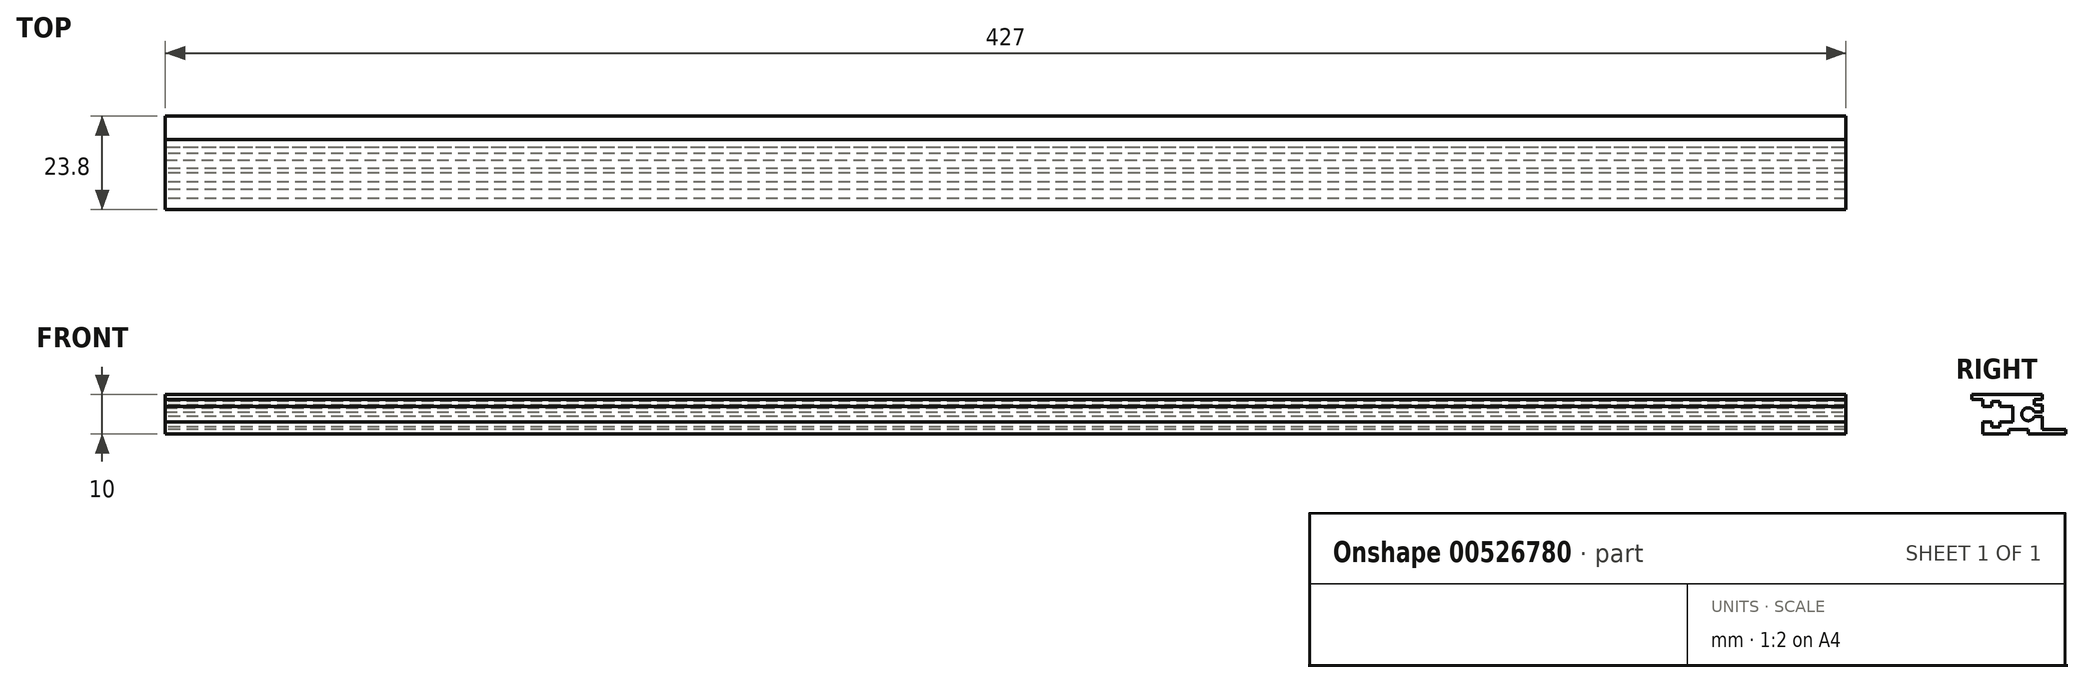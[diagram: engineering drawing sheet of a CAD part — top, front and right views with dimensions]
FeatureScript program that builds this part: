
annotation { "Feature Type Name" : "Feature", "Feature Type Description" : "" }
export const myFeature = defineFeature(function(context is Context, id is Id, definition is map)
    precondition{}
    {
        {
            assignVariable(context, id + "F0", {"name" : "length", "anyValue" : 427});
        }
        {
            var Q0;
            Q0=qCreatedBy(makeId("Right.planeOp"),FACE);
            var sketch = newSketch(context, id + "F1", { "sketchPlane" : qUnion([Q0])});
            skLineSegment(sketch, "E0.top", {"start": v(-37.38, 18.75) * mm, "end": v(-34.58, 18.75) * mm});
            skLineSegment(sketch, "E1", {"start": v(-37.38, 19.95) * mm, "end": v(-37.38, 18.75) * mm});
            skLineSegment(sketch, "E2.top", {"start": v(-13.58, 11.15) * mm, "end": v(-19.58, 11.15) * mm});
            skLineSegment(sketch, "E3", {"start": v(-37.38, 19.95) * mm, "end": v(-19.58, 19.95) * mm});
            skLineSegment(sketch, "E4", {"start": v(-13.58, 11.15) * mm, "end": v(-13.58, 9.95) * mm});
            skLineSegment(sketch, "E5.bottom", {"start": v(-19.58, 19.95) * mm, "end": v(-21.58, 19.95) * mm});
            skLineSegment(sketch, "E5.top", {"start": v(-19.58, 18.75) * mm, "end": v(-21.58, 18.75) * mm});
            skLineSegment(sketch, "E5.left", {"start": v(-19.58, 19.95) * mm, "end": v(-19.58, 18.75) * mm});
            skLineSegment(sketch, "E6.bottom", {"start": v(-21.58, 18.75) * mm, "end": v(-19.58, 18.75) * mm});
            skLineSegment(sketch, "E6.top", {"start": v(-21.58, 17.35) * mm, "end": v(-19.58, 17.35) * mm});
            skLineSegment(sketch, "E6.left", {"start": v(-21.58, 18.75) * mm, "end": v(-21.58, 17.35) * mm});
            skLineSegment(sketch, "E7.right", {"start": v(-26.98, 12.95) * mm, "end": v(-26.98, 16.95) * mm});
            skLineSegment(sketch, "E8", {"start": v(-34.58, 18.75) * mm, "end": v(-34.58, 16.95) * mm});
            skLineSegment(sketch, "E9.bottom", {"start": v(-34.58, 12.95) * mm, "end": v(-32.32, 12.95) * mm});
            skLineSegment(sketch, "E9.right", {"start": v(-32.32, 12.95) * mm, "end": v(-32.32, 11.7) * mm});
            skLineSegment(sketch, "E10.bottom", {"start": v(-32.32, 11.7) * mm, "end": v(-30.33, 11.7) * mm});
            skLineSegment(sketch, "E10.top", {"start": v(-32.32, 18.2) * mm, "end": v(-30.33, 18.2) * mm});
            skLineSegment(sketch, "E11", {"start": v(-34.58, 12.95) * mm, "end": v(-34.58, 9.95) * mm});
            skLineSegment(sketch, "E12", {"start": v(-34.58, 16.95) * mm, "end": v(-32.32, 16.95) * mm});
            skLineSegment(sketch, "E13", {"start": v(-26.98, 16.95) * mm, "end": v(-30.33, 16.95) * mm});
            skLineSegment(sketch, "E14", {"start": v(-32.32, 18.2) * mm, "end": v(-32.32, 16.95) * mm});
            skLineSegment(sketch, "E15", {"start": v(-26.98, 12.95) * mm, "end": v(-30.33, 12.95) * mm});
            skLineSegment(sketch, "E16", {"start": v(-30.33, 18.2) * mm, "end": v(-30.33, 16.95) * mm});
            skLineSegment(sketch, "E17", {"start": v(-30.33, 12.95) * mm, "end": v(-30.33, 11.7) * mm});
            skLineSegment(sketch, "E18.bottom", {"start": v(-19.58, 15.55) * mm, "end": v(-21.58, 15.55) * mm});
            skLineSegment(sketch, "E18.top", {"start": v(-19.58, 14.35) * mm, "end": v(-21.58, 14.35) * mm});
            skLineSegment(sketch, "E18.right", {"start": v(-21.58, 15.55) * mm, "end": v(-21.58, 14.35) * mm});
            skLineSegment(sketch, "E19", {"start": v(-19.58, 17.35) * mm, "end": v(-19.58, 15.55) * mm});
            skLineSegment(sketch, "E20", {"start": v(-19.58, 14.35) * mm, "end": v(-19.58, 11.15) * mm});
            skLineSegment(sketch, "E21.bottom", {"start": v(-13.58, 9.95) * mm, "end": v(-23.08, 9.95) * mm});
            skLineSegment(sketch, "E22.top", {"start": v(-23.08, 11.15) * mm, "end": v(-28.08, 11.15) * mm});
            skLineSegment(sketch, "E22.right", {"start": v(-28.08, 9.95) * mm, "end": v(-28.08, 11.15) * mm});
            skLineSegment(sketch, "E23", {"start": v(-34.58, 9.95) * mm, "end": v(-28.08, 9.95) * mm});
            skLineSegment(sketch, "E24", {"start": v(-23.08, 11.15) * mm, "end": v(-23.08, 9.95) * mm});
            skSolve(sketch);
        }
        {
            var Q0;
            Q0 = qSketchRegion(id + "F1", true);
            extrude(context, id + "F2", {"entities" : qUnion([Q0]), "depth" : (getVariable(context, 'length')) * mm, "offsetDistance" : 25 * mm});
        }
        {
            var Q0;
            Q0=makeQuery(id+"F2.opExtrude","CAP_FACE",FACE,{"disambiguationData":[OSD([sQuery(id+"F1.wireOp",EDGE,"E0.top"),sQuery(id+"F1.wireOp",EDGE,"E0.right"),sQuery(id+"F1.wireOp",EDGE,"E1"),sQuery(id+"F1.wireOp",EDGE,"7WjtD8Os-DvTV-xx7e-wsHr-O7i4Oa3QZQYs"),sQuery(id+"F1.wireOp",EDGE,"E2.top"),sQuery(id+"F1.wireOp",EDGE,"E3"),sQuery(id+"F1.wireOp",EDGE,"E4"),sQuery(id+"F1.wireOp",EDGE,"E5.bottom"),sQuery(id+"F1.wireOp",EDGE,"E5.left"),sQuery(id+"F1.wireOp",EDGE,"E6.bottom"),sQuery(id+"F1.wireOp",EDGE,"E6.top"),sQuery(id+"F1.wireOp",EDGE,"E6.left"),sQuery(id+"F1.wireOp",EDGE,"5xcxBood-YYAR-WB05-Kpwu-UJQrYywPCwEj")])],"isStart":false});
            var sketch = newSketch(context, id + "F3", { "sketchPlane" : qUnion([Q0])});
            skCircle(sketch, "E25", {"center": v(-23.08, 14.95) * mm, "radius": 1.65 * mm});
            skSolve(sketch);
        }
        {
            var Q0;
            Q0 = qSketchRegion(id + "F3", true);
            extrude(context, id + "F4", {"entities" : qUnion([Q0]), "operationType" : NewBodyOperationType.REMOVE, "oppositeDirection" : true, "depth" : (getVariable(context, 'length')) * mm, "offsetDistance" : 25 * mm});
        }
    });
